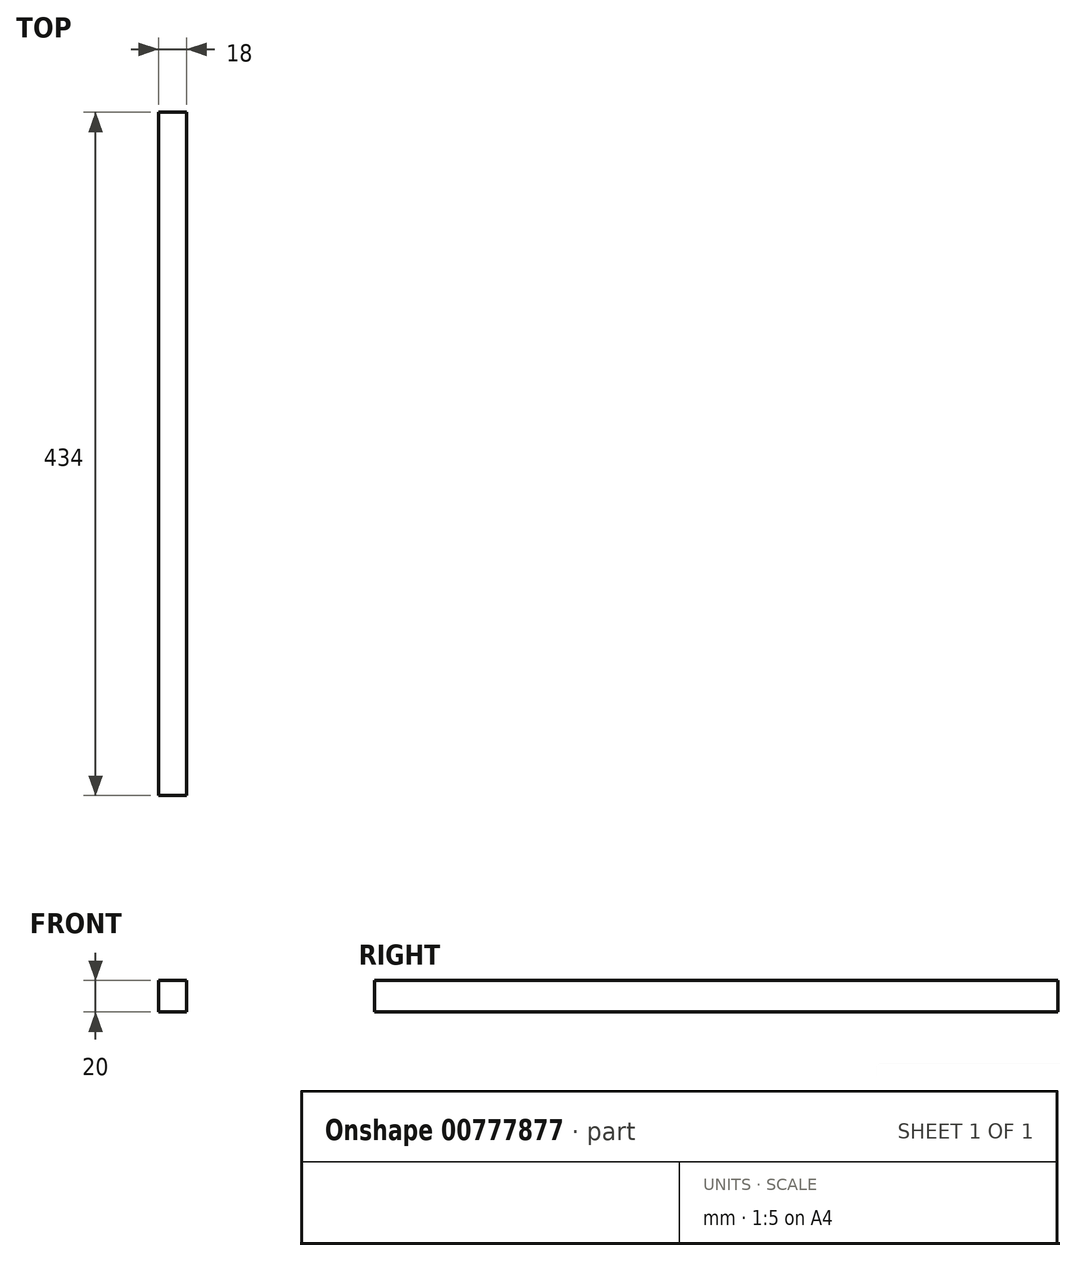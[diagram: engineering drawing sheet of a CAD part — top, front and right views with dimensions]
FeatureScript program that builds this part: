
annotation { "Feature Type Name" : "Feature", "Feature Type Description" : "" }
export const myFeature = defineFeature(function(context is Context, id is Id, definition is map)
    precondition{}
    {
        {
            var Q0;
            Q0=qCreatedBy(makeId("Top.planeOp"),FACE);
            var sketch = newSketch(context, id + "F0", { "sketchPlane" : qUnion([Q0])});
            skLineSegment(sketch, "E0.bottom", {"start": v(-9, 217) * mm, "end": v(9, 217) * mm});
            skLineSegment(sketch, "E0.top", {"start": v(-9, -217) * mm, "end": v(9, -217) * mm});
            skLineSegment(sketch, "E0.left", {"start": v(-9, 217) * mm, "end": v(-9, -217) * mm});
            skLineSegment(sketch, "E0.right", {"start": v(9, 217) * mm, "end": v(9, -217) * mm});
            skSolve(sketch);
        }
        {
            var Q0;
            Q0 = qSketchRegion(id + "F0", true);
            extrude(context, id + "F1", {"entities" : qUnion([Q0]), "endBound" : BoundingType.SYMMETRIC, "depth" : 20 * mm, "offsetDistance" : 25 * mm});
        }
    });
